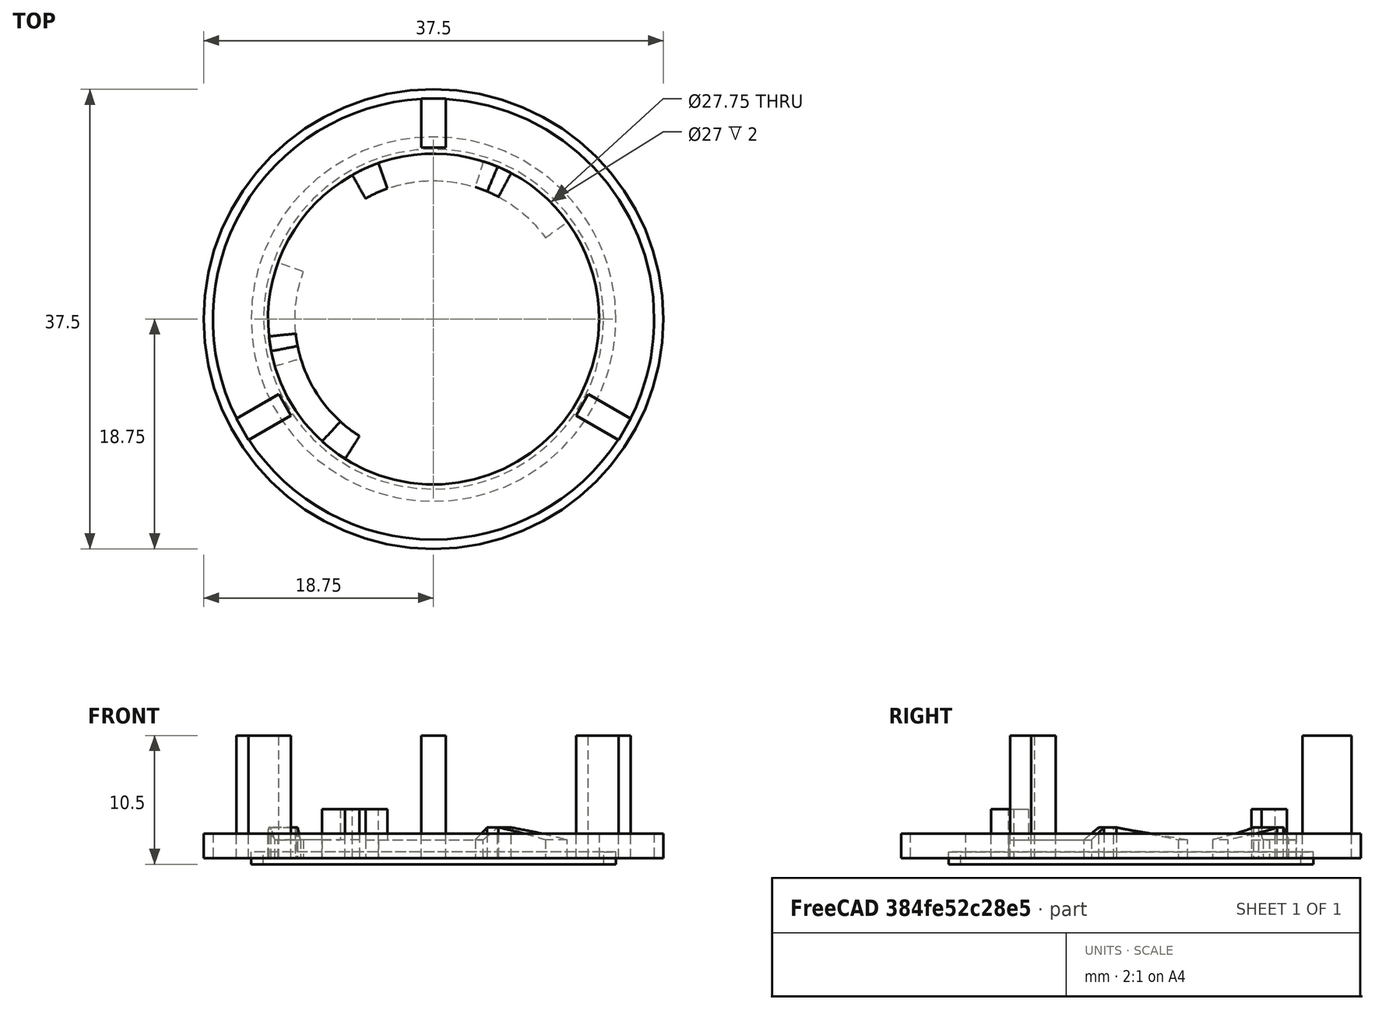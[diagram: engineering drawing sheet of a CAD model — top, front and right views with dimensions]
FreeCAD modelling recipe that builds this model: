
FCSTD DOCUMENT  (FreeCAD 0.19R21857 (Git))
Label: BayonetBaseFemaleV3
License: All rights reserved
LicenseURL: http://en.wikipedia.org/wiki/All_rights_reserved
objects: Sketcher::SketchObject×28, Part::Sweep×11, Part::MultiFuse×4, Part::Cylinder×3, Part::Mirroring×2, PartDesign::Body×1, Part::Cut×1, Part::Box×1, Part::FeaturePython×1, Image::ImagePlane×1
note: 52 computed .brp shape members not serialized (recipe doc carries the construction recipe); baked Part::Feature solids carry a one-line shape summary decoded from their .brp

FEATURE [Part::Cylinder] Cylinder
  Angle = 360
  AttacherType = Attacher::AttachEngine3D
  Height = 2
  Radius = 18.75
FEATURE [Sketcher::SketchObject] Sketch  label="RampStart"
  Placement = pos=(0,0,0) rot=(1,0,0;1.5708rad)
  sketch-geometry (4):
    g0: LineSegment StartX=-13.5 StartY=0 StartZ=0 EndX=-13.5 EndY=1.5 EndZ=0
    g1: LineSegment StartX=-13.5 StartY=1.5 StartZ=0 EndX=-11.3 EndY=1.5 EndZ=0
    g2: LineSegment StartX=-11.3 StartY=1.5 StartZ=0 EndX=-11.3 EndY=0 EndZ=0
    g3: LineSegment StartX=-11.3 StartY=0 StartZ=0 EndX=-13.5 EndY=0 EndZ=0
  constraints (12):
    c: Coincident(g0,g1)
    c: Coincident(g1,g2)
    c: Coincident(g2,g3)
    c: Coincident(g3,g0)
    c: Parallel(g0,g2)
    c: Parallel(g1,g3)
    c: Horizontal(g3)
    c: Vertical(g2)
    c: DistanceY(g-1,g2) = 0
    c: DistanceX(g2,g-1) = 11.3
    c: DistanceX(g0,g-1) = 13.5
    c: DistanceY(g0,g0) = 1.5
FEATURE [Sketcher::SketchObject] Sketch001  label="InnerCircumference"
  Placement = pos=(0,0,0) rot=(1,0,0;3.14159rad)
  sketch-geometry (1):
    g0: Circle CenterX=0 CenterY=0 CenterZ=0 NormalX=0 NormalY=0 NormalZ=1 AngleXU=0 Radius=11
  constraints (1):
    c: Radius(g0) = 11
FEATURE [Sketcher::SketchObject] Sketch002  label="RampEnd"
  Placement = pos=(0,0,0) rot=(0.950615,-0.219467,-0.219467;1.62142rad)
  sketch-geometry (4):
    g0: LineSegment StartX=-13.5 StartY=0 StartZ=0 EndX=-13.5 EndY=2.5 EndZ=0
    g1: LineSegment StartX=-13.5 StartY=2.5 StartZ=0 EndX=-11.3 EndY=2.5 EndZ=0
    g2: LineSegment StartX=-11.3 StartY=2.5 StartZ=0 EndX=-11.3 EndY=0 EndZ=0
    g3: LineSegment StartX=-11.3 StartY=0 StartZ=0 EndX=-13.5 EndY=0 EndZ=0
  constraints (12):
    c: Coincident(g0,g1)
    c: Coincident(g1,g2)
    c: Coincident(g2,g3)
    c: Coincident(g3,g0)
    c: Parallel(g0,g2)
    c: Parallel(g1,g3)
    c: Horizontal(g3)
    c: Vertical(g2)
    c: DistanceY(g-1,g2) = 0
    c: DistanceX(g2,g-1) = 11.3
    c: DistanceX(g0,g-1) = 13.5
    c: DistanceY(g0,g0) = 2.5
FEATURE [Sketcher::SketchObject] Sketch003  label="RampFlat"
  Placement = pos=(0,0,0) rot=(0.930118,-0.259693,-0.259693;1.64318rad)
  sketch-geometry (4):
    g0: LineSegment StartX=-13.5 StartY=0 StartZ=0 EndX=-13.5 EndY=2.5 EndZ=0
    g1: LineSegment StartX=-13.5 StartY=2.5 StartZ=0 EndX=-11.3 EndY=2.5 EndZ=0
    g2: LineSegment StartX=-11.3 StartY=2.5 StartZ=0 EndX=-11.3 EndY=0 EndZ=0
    g3: LineSegment StartX=-11.3 StartY=0 StartZ=0 EndX=-13.5 EndY=0 EndZ=0
  constraints (12):
    c: Coincident(g0,g1)
    c: Coincident(g1,g2)
    c: Coincident(g2,g3)
    c: Coincident(g3,g0)
    c: Parallel(g0,g2)
    c: Parallel(g1,g3)
    c: Horizontal(g3)
    c: Vertical(g2)
    c: DistanceY(g-1,g2) = 0
    c: DistanceX(g2,g-1) = 11.3
    c: DistanceX(g0,g-1) = 13.5
    c: DistanceY(g0,g0) = 2.5
FEATURE [Sketcher::SketchObject] Sketch004  label="LockFlat"
  Placement = pos=(0,0,0) rot=(0.906297,-0.298852,-0.298852;1.66903rad)
  sketch-geometry (4):
    g0: LineSegment StartX=-13.5 StartY=0 StartZ=0 EndX=-13.5 EndY=1.5 EndZ=0
    g1: LineSegment StartX=-13.5 StartY=1.5 StartZ=0 EndX=-11.3 EndY=1.5 EndZ=0
    g2: LineSegment StartX=-11.3 StartY=1.5 StartZ=0 EndX=-11.3 EndY=0 EndZ=0
    g3: LineSegment StartX=-11.3 StartY=0 StartZ=0 EndX=-13.5 EndY=0 EndZ=0
  constraints (12):
    c: Coincident(g0,g1)
    c: Coincident(g1,g2)
    c: Coincident(g2,g3)
    c: Coincident(g3,g0)
    c: Parallel(g0,g2)
    c: Parallel(g1,g3)
    c: Horizontal(g3)
    c: Vertical(g2)
    c: DistanceY(g-1,g2) = 0
    c: DistanceX(g2,g-1) = 11.3
    c: DistanceX(g0,g-1) = 13.5
    c: DistanceY(g0,g0) = 1.5
FEATURE [Sketcher::SketchObject] Sketch005  label="LockFlatEnd"
  Placement = pos=(0,0,0) rot=(0.621652,-0.553872,-0.553872;2.02922rad)
  sketch-geometry (4):
    g0: LineSegment StartX=-13.5 StartY=0 StartZ=0 EndX=-13.5 EndY=1.5 EndZ=0
    g1: LineSegment StartX=-13.5 StartY=1.5 StartZ=0 EndX=-11.3 EndY=1.5 EndZ=0
    g2: LineSegment StartX=-11.3 StartY=1.5 StartZ=0 EndX=-11.3 EndY=0 EndZ=0
    g3: LineSegment StartX=-11.3 StartY=0 StartZ=0 EndX=-13.5 EndY=0 EndZ=0
  constraints (12):
    c: Coincident(g0,g1)
    c: Coincident(g1,g2)
    c: Coincident(g2,g3)
    c: Coincident(g3,g0)
    c: Parallel(g0,g2)
    c: Parallel(g1,g3)
    c: Horizontal(g3)
    c: Vertical(g2)
    c: DistanceY(g-1,g2) = 0
    c: DistanceX(g2,g-1) = 11.3
    c: DistanceX(g0,g-1) = 13.5
    c: DistanceY(g0,g0) = 1.5
FEATURE [Sketcher::SketchObject] Sketch006  label="RampPath"
  sketch-geometry (1):
    g0: ArcOfCircle CenterX=0 CenterY=0 CenterZ=0 NormalX=0 NormalY=0 NormalZ=1 AngleXU=0 Radius=11.0109 StartAngle=1.68589 EndAngle=3.14182
FEATURE [Sketcher::SketchObject] Sketch007  label="Path1"
  sketch-geometry (2):
    g0: ArcOfCircle CenterX=0 CenterY=0 CenterZ=0 NormalX=0 NormalY=0 NormalZ=1 AngleXU=0 Radius=11.3 StartAngle=2.68754 EndAngle=3.14132
    g1: GeomPoint X=-10.1564 Y=4.95359 Z=0
  constraints (3):
    c: Radius(g0) = 11.3
    c: Coincident(g-1,g0)
    c: Angle(g0) = 0.453786
FEATURE [PartDesign::Body] Body
  Group = -> [Sketch005,Sketch004,Sketch003,Sketch002,Sketch001,Sketch,Sketch006,Sketch007]
  Origin = -> Origin
FEATURE [Part::Sweep] Sweep
  Frenet = false
  Sections = -> [Sketch,Sketch002]
  Solid = true
  Spine = -> Sketch007 [Edge1]
  Transition = 1
FEATURE [Sketcher::SketchObject] Sketch008  label="Path2"
  sketch-geometry (1):
    g0: ArcOfCircle CenterX=0 CenterY=0 CenterZ=0 NormalX=0 NormalY=0 NormalZ=1 AngleXU=0 Radius=11.3 StartAngle=2.59707 EndAngle=2.68754
  constraints (2):
    c: Radius(g0) = 11.3
    c: Coincident(g0,g-1)
FEATURE [Sketcher::SketchObject] Sketch009  label="Path3"
  sketch-geometry (1):
    g0: ArcOfCircle CenterX=0 CenterY=0 CenterZ=0 NormalX=0 NormalY=0 NormalZ=1 AngleXU=0 Radius=11.3 StartAngle=2.50468 EndAngle=2.59704
  constraints (2):
    c: Radius(g0) = 11.3
    c: Coincident(g0,g-1)
FEATURE [Sketcher::SketchObject] Sketch010  label="Path4"
  sketch-geometry (1):
    g0: ArcOfCircle CenterX=0 CenterY=0 CenterZ=0 NormalX=0 NormalY=0 NormalZ=1 AngleXU=0 Radius=11.3 StartAngle=1.68594 EndAngle=2.50452
  constraints (2):
    c: Radius(g0) = 11.3
    c: Coincident(g0,g-1)
FEATURE [Part::Sweep] Sweep001
  Frenet = false
  Sections = -> [Sketch002,Sketch003]
  Solid = true
  Spine = -> Sketch008 [Edge1]
  Transition = 1
FEATURE [Part::Sweep] Sweep002
  Frenet = false
  Sections = -> [Sketch003,Sketch004]
  Solid = true
  Spine = -> Sketch009 [Edge1]
  Transition = 1
FEATURE [Part::Sweep] Sweep003
  Frenet = false
  Sections = -> [Sketch004,Sketch005]
  Solid = true
  Spine = -> Sketch010 [Edge1]
  Transition = 1
FEATURE [Part::MultiFuse] Fusion  label="Ramp"
  Shapes = -> [Sweep,Sweep001,Sweep002,Sweep003]
FEATURE [Sketcher::SketchObject] Sketch011  label="EndstopEnd"
  Placement = pos=(0,0,0) rot=(0.621652,-0.553872,-0.553872;2.02922rad)
  sketch-geometry (4):
    g0: LineSegment StartX=-13.5 StartY=0 StartZ=0 EndX=-13.5 EndY=4 EndZ=0
    g1: LineSegment StartX=-13.5 StartY=4 StartZ=0 EndX=-11.3 EndY=4 EndZ=0
    g2: LineSegment StartX=-11.3 StartY=4 StartZ=0 EndX=-11.3 EndY=0 EndZ=0
    g3: LineSegment StartX=-11.3 StartY=0 StartZ=0 EndX=-13.5 EndY=0 EndZ=0
  constraints (12):
    c: Coincident(g0,g1)
    c: Coincident(g1,g2)
    c: Coincident(g2,g3)
    c: Coincident(g3,g0)
    c: Parallel(g0,g2)
    c: Parallel(g1,g3)
    c: Horizontal(g3)
    c: Vertical(g2)
    c: DistanceY(g-1,g2) = 0
    c: DistanceX(g2,g-1) = 11.3
    c: DistanceX(g0,g-1) = 13.5
    c: DistanceY(g0,g0) = 4
FEATURE [Sketcher::SketchObject] Sketch012  label="EndstopStart"
  Placement = pos=(0,0,0) rot=(0.688237,-0.512996,-0.512996;1.93602rad)
  sketch-geometry (4):
    g0: LineSegment StartX=-13.5 StartY=0 StartZ=0 EndX=-13.5 EndY=4 EndZ=0
    g1: LineSegment StartX=-13.5 StartY=4 StartZ=0 EndX=-11.3 EndY=4 EndZ=0
    g2: LineSegment StartX=-11.3 StartY=4 StartZ=0 EndX=-11.3 EndY=0 EndZ=0
    g3: LineSegment StartX=-11.3 StartY=0 StartZ=0 EndX=-13.5 EndY=0 EndZ=0
  constraints (12):
    c: Coincident(g0,g1)
    c: Coincident(g1,g2)
    c: Coincident(g2,g3)
    c: Coincident(g3,g0)
    c: Parallel(g0,g2)
    c: Parallel(g1,g3)
    c: Horizontal(g3)
    c: Vertical(g2)
    c: DistanceY(g-1,g2) = 0
    c: DistanceX(g2,g-1) = 11.3
    c: DistanceX(g0,g-1) = 13.5
    c: DistanceY(g0,g0) = 4
FEATURE [Sketcher::SketchObject] Sketch013  label="EndstopPath"
  sketch-geometry (1):
    g0: ArcOfCircle CenterX=0 CenterY=0 CenterZ=0 NormalX=0 NormalY=0 NormalZ=1 AngleXU=0 Radius=11.3 StartAngle=1.68607 EndAngle=1.86043
  constraints (2):
    c: Radius(g0) = 11.3
    c: Coincident(g-1,g0)
FEATURE [Part::Sweep] Sweep004  label="EndStop"
  Frenet = false
  Sections = -> [Sketch012,Sketch011]
  Solid = true
  Spine = -> Sketch013 [Edge1]
  Transition = 1
FEATURE [Part::MultiFuse] Fusion001  label="RampWithEndstop"
  Shapes = -> [Fusion,Sweep004]
FEATURE [Part::Cylinder] Cylinder001
  Angle = 360
  AttacherType = Attacher::AttachEngine3D
  Height = 2
  Radius = 18
FEATURE [Part::Cylinder] Cylinder002
  Angle = 360
  AttacherType = Attacher::AttachEngine3D
  Height = 2
  Radius = 13.5
FEATURE [Part::Cut] Cut  label="Base"
  Base = -> Cylinder001
  Placement = pos=(0,0,2) rot=(1,0,0;3.14159rad)
  Tool = -> Cylinder002
FEATURE [Sketcher::SketchObject] Sketch015  label="GrooveProfile"
  Placement = pos=(0,0,0) rot=(1,0,0;1.5708rad)
  sketch-geometry (4):
    g0: LineSegment StartX=-14.875 StartY=-0.5 StartZ=0 EndX=-13.875 EndY=-0.5 EndZ=0
    g1: LineSegment StartX=-13.875 StartY=-0.5 StartZ=0 EndX=-13.875 EndY=0.5 EndZ=0
    g2: LineSegment StartX=-13.875 StartY=0.5 StartZ=0 EndX=-14.875 EndY=0.5 EndZ=0
    g3: LineSegment StartX=-14.875 StartY=0.5 StartZ=0 EndX=-14.875 EndY=-0.5 EndZ=0
  constraints (12):
    c: Coincident(g0,g1)
    c: Coincident(g1,g2)
    c: Coincident(g2,g3)
    c: Coincident(g3,g0)
    c: Horizontal(g0)
    c: Horizontal(g2)
    c: Vertical(g1)
    c: Vertical(g3)
    c: DistanceX(g0,g0) = 1
    c: Equal(g0,g1)
    c: DistanceY(g1,g-1) = -0.5
    c: DistanceX(g1,g-1) = 13.875
FEATURE [Sketcher::SketchObject] Sketch016  label="GroovePath"
  sketch-geometry (1):
    g0: Circle CenterX=0 CenterY=0 CenterZ=0 NormalX=0 NormalY=0 NormalZ=1 AngleXU=0 Radius=13.875
  constraints (2):
    c: Coincident(g0,g-1)
    c: Radius(g0) = 13.875
FEATURE [Part::Sweep] Sweep005  label="Groove"
  Frenet = false
  Sections = -> [Sketch015]
  Solid = true
  Spine = -> Sketch016 [Edge1]
  Transition = 1
FEATURE [Part::Box] Box  label="Cube"
  AttacherType = Attacher::AttachEngine3D
  Height = 10
  Length = 2
  Placement = pos=(-1,14,0) rot=(0,0,1;0rad)
  Width = 4
FEATURE [Part::FeaturePython] Array001  label="Testhandles"  # Draft array (typed FeaturePython)
  Angle = 360
  ArrayType = 1
  Axis = (0,0,1)
  Base = -> Box
  Center = (0,0,0)
  Fuse = false
  IntervalAxis = (0,0,0)
  IntervalX = (1,0,0)
  IntervalY = (0,1,0)
  IntervalZ = (0,0,1)
  NumberPolar = 3
  NumberX = 0
  NumberY = 0
  NumberZ = 0
FEATURE [Part::Mirroring] Part__Mirroring  label="RampWithEndstop (Mirror #1)"
  Base = (0,0,0)
  Normal = (0,1,0)
  Placement = pos=(0,0,0) rot=(0,0,1;3.76991rad)
  Source = -> Fusion001
FEATURE [Image::ImagePlane] ImagePlane
  Placement = pos=(0.5,6,2) rot=(0,1,0;3.14159rad)
  XSize = 50.7829
  YSize = 59.8109
FEATURE [Sketcher::SketchObject] Sketch017  label="RampStart001"
  Placement = pos=(0,0,0) rot=(1,0,0;1.5708rad)
  sketch-geometry (4):
    g0: LineSegment StartX=-13.5 StartY=0 StartZ=0 EndX=-13.5 EndY=1.5 EndZ=0
    g1: LineSegment StartX=-13.5 StartY=1.5 StartZ=0 EndX=-11.3 EndY=1.5 EndZ=0
    g2: LineSegment StartX=-11.3 StartY=1.5 StartZ=0 EndX=-11.3 EndY=0 EndZ=0
    g3: LineSegment StartX=-11.3 StartY=0 StartZ=0 EndX=-13.5 EndY=0 EndZ=0
  constraints (12):
    c: Coincident(g0,g1)
    c: Coincident(g1,g2)
    c: Coincident(g2,g3)
    c: Coincident(g3,g0)
    c: Parallel(g0,g2)
    c: Parallel(g1,g3)
    c: Horizontal(g3)
    c: Vertical(g2)
    c: DistanceY(g-1,g2) = 0
    c: DistanceX(g2,g-1) = 11.3
    c: DistanceX(g0,g-1) = 13.5
    c: DistanceY(g0,g0) = 1.5
FEATURE [Sketcher::SketchObject] Sketch018  label="RampEnd001"
  Placement = pos=(0,0,0) rot=(0.950615,-0.219467,-0.219467;1.62142rad)
  sketch-geometry (4):
    g0: LineSegment StartX=-13.5 StartY=0 StartZ=0 EndX=-13.5 EndY=2.5 EndZ=0
    g1: LineSegment StartX=-13.5 StartY=2.5 StartZ=0 EndX=-11.3 EndY=2.5 EndZ=0
    g2: LineSegment StartX=-11.3 StartY=2.5 StartZ=0 EndX=-11.3 EndY=0 EndZ=0
    g3: LineSegment StartX=-11.3 StartY=0 StartZ=0 EndX=-13.5 EndY=0 EndZ=0
  constraints (12):
    c: Coincident(g0,g1)
    c: Coincident(g1,g2)
    c: Coincident(g2,g3)
    c: Coincident(g3,g0)
    c: Parallel(g0,g2)
    c: Parallel(g1,g3)
    c: Horizontal(g3)
    c: Vertical(g2)
    c: DistanceY(g-1,g2) = 0
    c: DistanceX(g2,g-1) = 11.3
    c: DistanceX(g0,g-1) = 13.5
    c: DistanceY(g0,g0) = 2.5
FEATURE [Sketcher::SketchObject] Sketch019  label="RampFlat001"
  Placement = pos=(0,0,0) rot=(0.930118,-0.259693,-0.259693;1.64318rad)
  sketch-geometry (4):
    g0: LineSegment StartX=-13.5 StartY=0 StartZ=0 EndX=-13.5 EndY=2.5 EndZ=0
    g1: LineSegment StartX=-13.5 StartY=2.5 StartZ=0 EndX=-11.3 EndY=2.5 EndZ=0
    g2: LineSegment StartX=-11.3 StartY=2.5 StartZ=0 EndX=-11.3 EndY=0 EndZ=0
    g3: LineSegment StartX=-11.3 StartY=0 StartZ=0 EndX=-13.5 EndY=0 EndZ=0
  constraints (12):
    c: Coincident(g0,g1)
    c: Coincident(g1,g2)
    c: Coincident(g2,g3)
    c: Coincident(g3,g0)
    c: Parallel(g0,g2)
    c: Parallel(g1,g3)
    c: Horizontal(g3)
    c: Vertical(g2)
    c: DistanceY(g-1,g2) = 0
    c: DistanceX(g2,g-1) = 11.3
    c: DistanceX(g0,g-1) = 13.5
    c: DistanceY(g0,g0) = 2.5
FEATURE [Sketcher::SketchObject] Sketch020  label="LockFlat001"
  Placement = pos=(0,0,0) rot=(0.906297,-0.298852,-0.298852;1.66903rad)
  sketch-geometry (4):
    g0: LineSegment StartX=-13.5 StartY=0 StartZ=0 EndX=-13.5 EndY=1.5 EndZ=0
    g1: LineSegment StartX=-13.5 StartY=1.5 StartZ=0 EndX=-11.3 EndY=1.5 EndZ=0
    g2: LineSegment StartX=-11.3 StartY=1.5 StartZ=0 EndX=-11.3 EndY=0 EndZ=0
    g3: LineSegment StartX=-11.3 StartY=0 StartZ=0 EndX=-13.5 EndY=0 EndZ=0
  constraints (12):
    c: Coincident(g0,g1)
    c: Coincident(g1,g2)
    c: Coincident(g2,g3)
    c: Coincident(g3,g0)
    c: Parallel(g0,g2)
    c: Parallel(g1,g3)
    c: Horizontal(g3)
    c: Vertical(g2)
    c: DistanceY(g-1,g2) = 0
    c: DistanceX(g2,g-1) = 11.3
    c: DistanceX(g0,g-1) = 13.5
    c: DistanceY(g0,g0) = 1.5
FEATURE [Sketcher::SketchObject] Sketch021  label="LockFlatEnd001"
  Placement = pos=(0,0,0) rot=(0.659735,-0.531389,-0.531389;1.97521rad)
  sketch-geometry (4):
    g0: LineSegment StartX=-13.5 StartY=0 StartZ=0 EndX=-13.5 EndY=1.5 EndZ=0
    g1: LineSegment StartX=-13.5 StartY=1.5 StartZ=0 EndX=-11.3 EndY=1.5 EndZ=0
    g2: LineSegment StartX=-11.3 StartY=1.5 StartZ=0 EndX=-11.3 EndY=0 EndZ=0
    g3: LineSegment StartX=-11.3 StartY=0 StartZ=0 EndX=-13.5 EndY=0 EndZ=0
  constraints (12):
    c: Coincident(g0,g1)
    c: Coincident(g1,g2)
    c: Coincident(g2,g3)
    c: Coincident(g3,g0)
    c: Parallel(g0,g2)
    c: Parallel(g1,g3)
    c: Horizontal(g3)
    c: Vertical(g2)
    c: DistanceY(g-1,g2) = 0
    c: DistanceX(g2,g-1) = 11.3
    c: DistanceX(g0,g-1) = 13.5
    c: DistanceY(g0,g0) = 1.5
FEATURE [Sketcher::SketchObject] Sketch022  label="Path005"
  sketch-geometry (2):
    g0: ArcOfCircle CenterX=0 CenterY=0 CenterZ=0 NormalX=0 NormalY=0 NormalZ=1 AngleXU=0 Radius=11.3 StartAngle=2.68754 EndAngle=3.14132
    g1: GeomPoint X=-10.1564 Y=4.95359 Z=0
  constraints (3):
    c: Radius(g0) = 11.3
    c: Coincident(g-1,g0)
    c: Angle(g0) = 0.453786
FEATURE [Part::Sweep] Sweep006
  Frenet = false
  Sections = -> [Sketch017,Sketch018]
  Solid = true
  Spine = -> Sketch022 [Edge1]
  Transition = 1
FEATURE [Sketcher::SketchObject] Sketch023  label="Path006"
  sketch-geometry (1):
    g0: ArcOfCircle CenterX=0 CenterY=0 CenterZ=0 NormalX=0 NormalY=0 NormalZ=1 AngleXU=0 Radius=11.3 StartAngle=2.59707 EndAngle=2.68754
  constraints (2):
    c: Radius(g0) = 11.3
    c: Coincident(g0,g-1)
FEATURE [Sketcher::SketchObject] Sketch024  label="Path007"
  sketch-geometry (1):
    g0: ArcOfCircle CenterX=0 CenterY=0 CenterZ=0 NormalX=0 NormalY=0 NormalZ=1 AngleXU=0 Radius=11.3 StartAngle=2.50468 EndAngle=2.59704
  constraints (2):
    c: Radius(g0) = 11.3
    c: Coincident(g0,g-1)
FEATURE [Sketcher::SketchObject] Sketch025  label="Path008"
  sketch-geometry (1):
    g0: ArcOfCircle CenterX=0 CenterY=0 CenterZ=0 NormalX=0 NormalY=0 NormalZ=1 AngleXU=0 Radius=11.3 StartAngle=1.78537 EndAngle=2.50452
  constraints (2):
    c: Radius(g0) = 11.3
    c: Coincident(g0,g-1)
FEATURE [Part::Sweep] Sweep007
  Frenet = false
  Sections = -> [Sketch019,Sketch020]
  Solid = true
  Spine = -> Sketch024 [Edge1]
  Transition = 1
FEATURE [Part::Sweep] Sweep008
  Frenet = false
  Sections = -> [Sketch020,Sketch021]
  Solid = true
  Spine = -> Sketch025 [Edge1]
  Transition = 1
FEATURE [Sketcher::SketchObject] Sketch026  label="EndstopEnd001"
  Placement = pos=(0,0,0) rot=(0.659735,-0.531389,-0.531389;1.97521rad)
  sketch-geometry (4):
    g0: LineSegment StartX=-13.5 StartY=0 StartZ=0 EndX=-13.5 EndY=4 EndZ=0
    g1: LineSegment StartX=-13.5 StartY=4 StartZ=0 EndX=-11.3 EndY=4 EndZ=0
    g2: LineSegment StartX=-11.3 StartY=4 StartZ=0 EndX=-11.3 EndY=0 EndZ=0
    g3: LineSegment StartX=-11.3 StartY=0 StartZ=0 EndX=-13.5 EndY=0 EndZ=0
  constraints (12):
    c: Coincident(g0,g1)
    c: Coincident(g1,g2)
    c: Coincident(g2,g3)
    c: Coincident(g3,g0)
    c: Parallel(g0,g2)
    c: Parallel(g1,g3)
    c: Horizontal(g3)
    c: Vertical(g2)
    c: DistanceY(g-1,g2) = 0
    c: DistanceX(g2,g-1) = 11.3
    c: DistanceX(g0,g-1) = 13.5
    c: DistanceY(g0,g0) = 4
FEATURE [Sketcher::SketchObject] Sketch027  label="EndstopStart001"
  Placement = pos=(0,0,0) rot=(0.725535,-0.486621,-0.486621;1.88627rad)
  sketch-geometry (4):
    g0: LineSegment StartX=-13.5 StartY=0 StartZ=0 EndX=-13.5 EndY=4 EndZ=0
    g1: LineSegment StartX=-13.5 StartY=4 StartZ=0 EndX=-11.3 EndY=4 EndZ=0
    g2: LineSegment StartX=-11.3 StartY=4 StartZ=0 EndX=-11.3 EndY=0 EndZ=0
    g3: LineSegment StartX=-11.3 StartY=0 StartZ=0 EndX=-13.5 EndY=0 EndZ=0
  constraints (12):
    c: Coincident(g0,g1)
    c: Coincident(g1,g2)
    c: Coincident(g2,g3)
    c: Coincident(g3,g0)
    c: Parallel(g0,g2)
    c: Parallel(g1,g3)
    c: Horizontal(g3)
    c: Vertical(g2)
    c: DistanceY(g-1,g2) = 0
    c: DistanceX(g2,g-1) = 11.3
    c: DistanceX(g0,g-1) = 13.5
    c: DistanceY(g0,g0) = 4
FEATURE [Sketcher::SketchObject] Sketch028  label="EndstopPath001"
  sketch-geometry (1):
    g0: ArcOfCircle CenterX=0 CenterY=0 CenterZ=0 NormalX=0 NormalY=0 NormalZ=1 AngleXU=0 Radius=11.3 StartAngle=1.78561 EndAngle=1.95957
  constraints (2):
    c: Radius(g0) = 11.3
    c: Coincident(g-1,g0)
FEATURE [Part::Sweep] Sweep009  label="EndStop001"
  Frenet = false
  Sections = -> [Sketch027,Sketch026]
  Solid = true
  Spine = -> Sketch028 [Edge1]
  Transition = 1
FEATURE [Part::Sweep] Sweep010
  Frenet = false
  Sections = -> [Sketch018,Sketch019]
  Solid = true
  Spine = -> Sketch023 [Edge1]
  Transition = 1
FEATURE [Part::MultiFuse] Fusion002  label="Ramp001"
  Shapes = -> [Sweep006,Sweep010,Sweep007,Sweep008]
FEATURE [Part::MultiFuse] Fusion003  label="RampWithEndstopShort"
  Shapes = -> [Fusion002,Sweep009]
FEATURE [Part::Mirroring] Part__Mirroring001  label="RampWithEndstopShort (Mirror #2)"
  Base = (0,0,0)
  Normal = (0,1,0)
  Placement = pos=(0,0,0) rot=(0,0,1;5.93412rad)
  Source = -> Fusion003
